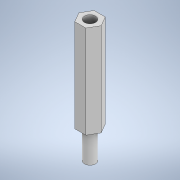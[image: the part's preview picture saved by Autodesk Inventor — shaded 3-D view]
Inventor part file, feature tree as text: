
AUTODESK INVENTOR PART (.ipt)
format: ipt  version: 2022 (Build 260153000, 153)  size: 109,568 bytes
history: native  units: mm
features: sketch x4, extrude x3
ambient origin geometry x8: Origin, YZ Plane, XZ Plane, XY Plane, X Axis, Y Axis, Z Axis, Center Point
bodies: Solid1 (feature_tree)
feature tree (7):
  sketch  "Sketch1"  dims[d0=6.0mm d1=25.0mm d2=0.0mm]
  sketch  "Sketch2"  dims[d3=3.0mm d4=3.0mm]
  extrude  "Extrusion1"  Depth=25.0mm TaperAngle=0.0deg
  sketch  "Sketch3"  dims[d5=8.0mm d6=0.0mm d7=10.0mm d8=0.0mm]
  sketch  "Sketch4"
  extrude  "Extrusion2"  Depth=3.0mm
  extrude  "Extrusion3"  Depth=10.0mm TaperAngle=0.0deg
